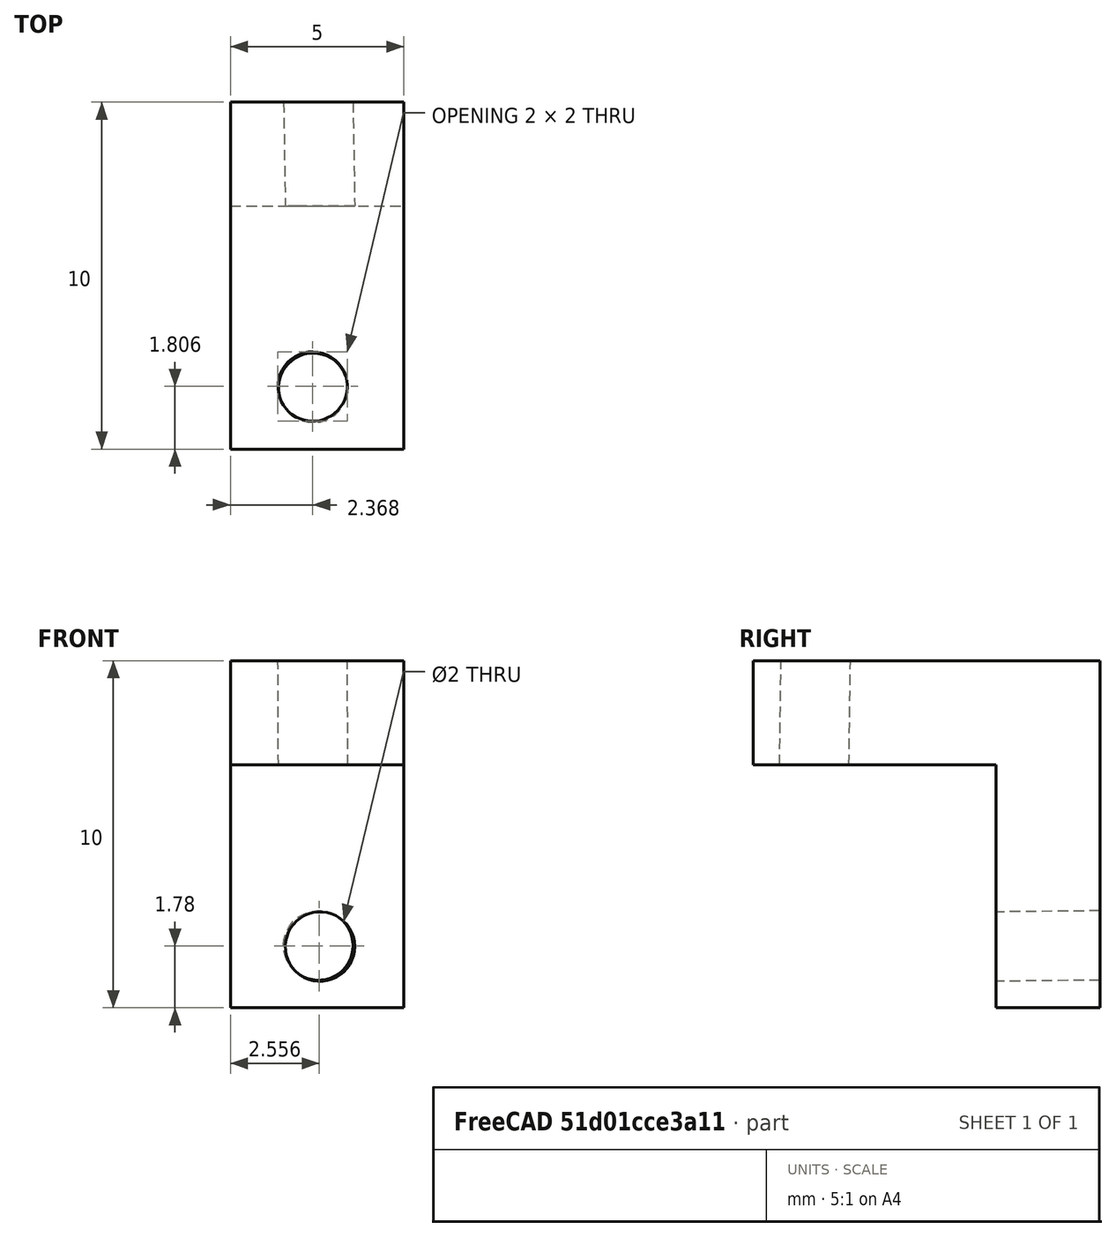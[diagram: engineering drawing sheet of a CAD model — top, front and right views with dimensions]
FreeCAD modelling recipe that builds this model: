
FCSTD DOCUMENT  (FreeCAD 0.16R6700 (Git))
Label: L Bracket 2 (connected)
License: All rights reserved
LicenseURL: http://en.wikipedia.org/wiki/All_rights_reserved
objects: Part::FeaturePython×3, Part::Box×2, Part::Cylinder×2
note: 7 computed .brp shape members not serialized (recipe doc carries the construction recipe); baked Part::Feature solids carry a one-line shape summary decoded from their .brp

FEATURE [Part::Box] Box  label="Vertical Cube"
  Height = 10
  Length = 5
  Width = 3
FEATURE [Part::Box] Box001  label="Top Cube"
  Height = 3
  Length = 10
  Placement = pos=(5,-7,7) rot=(0,0,1;1.5708rad)
  Width = 5
FEATURE [Part::Cylinder] Cylinder  label="Screw Hole"
  Angle = 360
  Height = 5
  Placement = pos=(2.51433,4.11494,1.80883) rot=(0.325907,0.674751,-0.66219;2.4989rad)
  Radius = 1
FEATURE [Part::Cylinder] Cylinder001  label="Screw Hole 2"
  Angle = 360
  Height = 5
  Placement = pos=(2.38593,-5.2465,6.00193) rot=(-0.365562,-0.131275,-0.921483;0.03575rad)
  Radius = 1
FEATURE [Part::FeaturePython] Cutout  # WARN: FeaturePython — macro-defined, semantics opaque (R4)
  Base = -> Box001
  Mode = 3
  Tool = -> Cylinder001
FEATURE [Part::FeaturePython] Cutout001  # WARN: FeaturePython — macro-defined, semantics opaque (R4)
  Base = -> Box
  Mode = 3
  Tool = -> Cylinder
FEATURE [Part::FeaturePython] Connect  # WARN: FeaturePython — macro-defined, semantics opaque (R4)
  Base = -> Cutout
  Mode = 1
  Tool = -> Cutout001
